# Revit family: Conveyor Idler_Figure 12_Face Base
name_source: partatom
category: Mechanical Equipment
revit_build: Autodesk Revit 2017 (Build: 20171027_0315(x64)
units: mm (PartAtom-declared; Revit-internal decimal feet)

## family parameters
Cut with Voids When Loaded = No
Host = Face
OmniClass Number = 23.50.30.24.37
Part Type = Normal
Room Calculation Point = No
Round Connector Dimension = Use Diameter
Shared = No

## types (1)
- Figure 12
    A = 355 mm
    A1 = 385 mm  [stored 1.26312 ft]
    Angle Offset = 0 mm  [stored 0 ft]
    B = 1800 mm  [stored 5.90551 ft]
    Belt Width = 0 mm  [stored 0 ft]
    Bracket AA Distance = 0 mm  [stored 0 ft]
    Bracket Thickness = 15 mm  [stored 0.0492126 ft]
    D = 0 mm  [stored 0 ft]
    Default Elevation = 1219 mm
    E = 110 mm  [stored 0.360892 ft]
    F = 350 mm  [stored 1.14829 ft]
    Frame Length = 2030 mm  [stored 6.6601 ft]
    G = 0 mm  [stored 0 ft]
    G1 = 0 mm  [stored 0 ft]
    Maximum Ore Particle Size = 0 mm  [stored 0 ft]
    Return Idler Spacing - Convex = 0 mm  [stored 0 ft]
    Return Idler Spacing - Heavy Duty = 0 mm  [stored 0 ft]
    Return Idler Spacing - Module = 0 mm  [stored 0 ft]
    Return Idler Spacing - Truss = 0 mm  [stored 0 ft]
    Roll A_Bracket Offset = 15 mm  [stored 0.0492126 ft]
    Roll G_Bracket Offset = 0 mm  [stored 0 ft]
    Roller AA_Hyp = 390 mm
    Roller AA_X-axis = 387 mm
    Roller AA_Y-axis = 51 mm
    Y = 35 mm  [stored 0.114829 ft]
    dia_Roll_A = 178 mm  [stored 0.58399 ft]
    dia_Roll_G = 0 mm  [stored 0 ft]
    x_angle_AA = 7.50°
    x_angle_AAA = 15.00°
    xdeg = 7.50°

note: [stored X ft] marks values corroborated as IEEE doubles in the binary element streams (Revit-internal decimal feet)

## geometry (parser evidence)
native form markers: Blend x2, Sweep x29
no freeform markers — native parametric forms only
